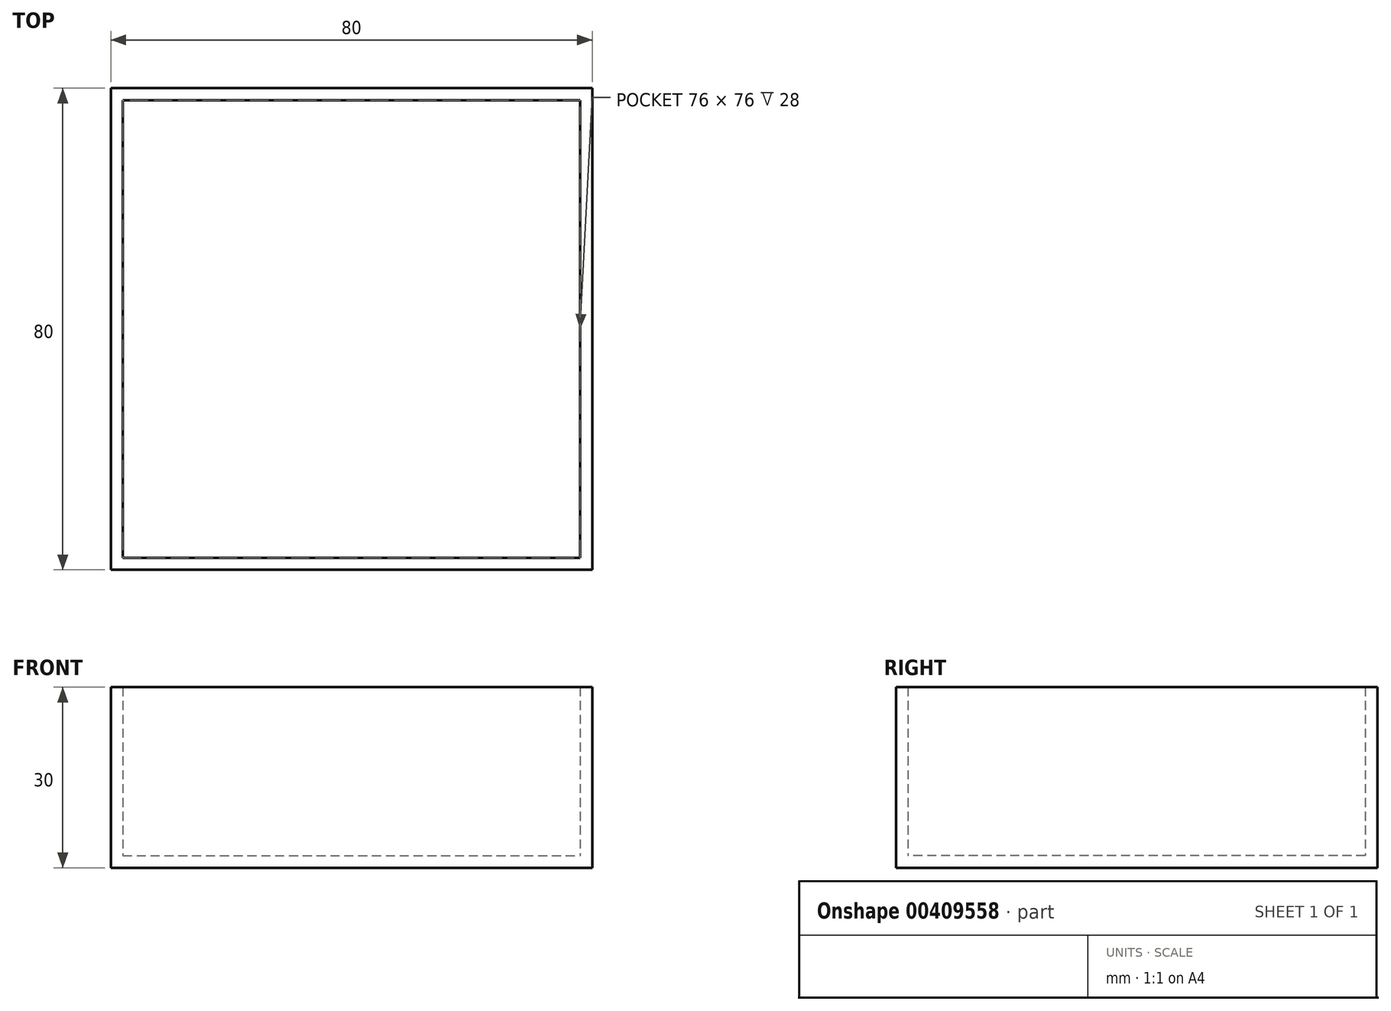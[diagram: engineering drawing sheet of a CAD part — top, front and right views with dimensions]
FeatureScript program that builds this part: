
annotation { "Feature Type Name" : "Feature", "Feature Type Description" : "" }
export const myFeature = defineFeature(function(context is Context, id is Id, definition is map)
    precondition{}
    {
        {
            var Q0;
            Q0=qCreatedBy(makeId("Top.planeOp"),FACE);
            var sketch = newSketch(context, id + "F0", { "sketchPlane" : qUnion([Q0])});
            skLineSegment(sketch, "E0.bottom", {"start": v(-40, 40) * mm, "end": v(40, 40) * mm});
            skLineSegment(sketch, "E0.top", {"start": v(-40, -40) * mm, "end": v(40, -40) * mm});
            skLineSegment(sketch, "E0.left", {"start": v(-40, 40) * mm, "end": v(-40, -40) * mm});
            skLineSegment(sketch, "E0.right", {"start": v(40, 40) * mm, "end": v(40, -40) * mm});
            skLineSegment(sketch, "E1", {"start": v(0, 40) * mm, "end": v(0, -40) * mm, "construction": true});
            skLineSegment(sketch, "E2", {"start": v(-40, 0) * mm, "end": v(40, 0) * mm, "construction": true});
            skSolve(sketch);
        }
        {
            var Q0;
            Q0=makeQuery(id+"F0.imprint","IMPRINT",FACE,{"disambiguationData":[TD([[makeQuery(id+"F0.imprint","IMPRINT",EDGE,{"derivedFrom":sQuery(id+"F0.wireOp",EDGE,"E0.bottom")}),-1.0]])]});
            extrude(context, id + "F1", {"entities" : qUnion([Q0]), "depth" : 30 * mm});
        }
        {
            var Q0;
            Q0=makeQuery(id+"F1.opExtrude","CAP_FACE",FACE,{"disambiguationData":[OSD([sQuery(id+"F0.wireOp",EDGE,"E0.bottom"),sQuery(id+"F0.wireOp",EDGE,"E0.top"),sQuery(id+"F0.wireOp",EDGE,"E0.left"),sQuery(id+"F0.wireOp",EDGE,"E0.right")])],"isStart":false});
            shell(context, id + "F2", {"entities" : qUnion([Q0]), "thickness" : 2 * mm});
        }
    });
